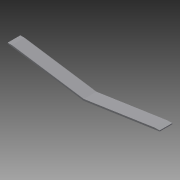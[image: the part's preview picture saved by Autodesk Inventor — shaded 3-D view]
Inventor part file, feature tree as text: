
AUTODESK INVENTOR PART (.ipt)
format: ipt  version: 2013 (Build 170138000, 138)  size: 88,576 bytes
history: native  units: in
note: dims shown in document units (in); Inventor stores cm internally (conversion verified against a paired STEP export)
features: extrude x2, sketch x2
ambient origin geometry x8: Origin, YZ Plane, XZ Plane, XY Plane, X Axis, Y Axis, Z Axis, Center Point
bodies: Solid1 (feature_tree)
feature tree (4):
  extrude  "Extrusion1"  Depth=12.0in
  extrude  "Extrusion2"  Depth=0.125in
  sketch  "Sketch1"  dims[d0=0.9in d2=12.0in]
  sketch  "Sketch2"  dims[d3=90.0deg d4=0.125in d5=0.125in d6=1.0in d7=0.0in d8=0.5in d9=0.051in d10=0.051in d11=2.0in d12=0.0in]
